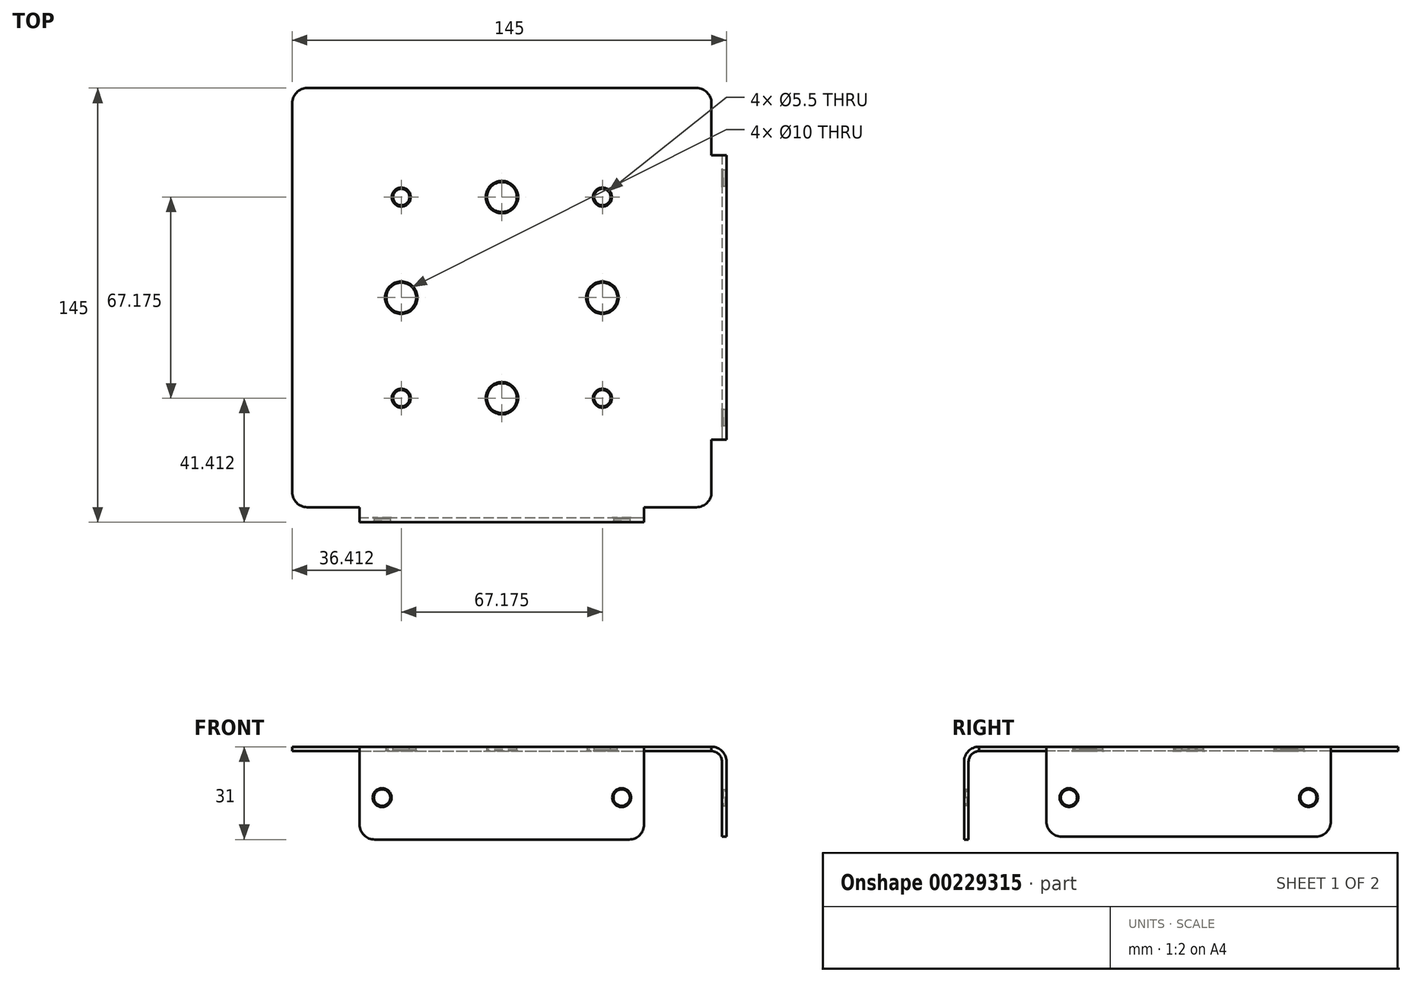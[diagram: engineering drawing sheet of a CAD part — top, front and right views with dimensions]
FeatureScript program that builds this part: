
annotation { "Feature Type Name" : "Feature", "Feature Type Description" : "" }
export const myFeature = defineFeature(function(context is Context, id is Id, definition is map)
    precondition{}
    {
        {
            var Q0;
            Q0=qCreatedBy(makeId("Top.planeOp"),FACE);
            var sketch = newSketch(context, id + "F0", { "sketchPlane" : qUnion([Q0])});
            skLineSegment(sketch, "E0.bottom", {"start": v(-70, 70) * mm, "end": v(70, 70) * mm});
            skLineSegment(sketch, "E0.top", {"start": v(-70, -70) * mm, "end": v(70, -70) * mm});
            skLineSegment(sketch, "E0.left", {"start": v(-70, 70) * mm, "end": v(-70, -70) * mm});
            skLineSegment(sketch, "E0.right", {"start": v(70, 70) * mm, "end": v(70, -70) * mm});
            skPoint(sketch, "E0.middle", {"position": v(0, 0) * mm});
            skLineSegment(sketch, "E1.bottom", {"start": v(-47.5, -70) * mm, "end": v(47.5, -70) * mm});
            skLineSegment(sketch, "E1.top", {"start": v(-47.5, -75) * mm, "end": v(47.5, -75) * mm});
            skLineSegment(sketch, "E1.left", {"start": v(-47.5, -70) * mm, "end": v(-47.5, -75) * mm});
            skLineSegment(sketch, "E1.right", {"start": v(47.5, -70) * mm, "end": v(47.5, -75) * mm});
            skLineSegment(sketch, "E2", {"start": v(70, -70) * mm, "end": v(0, 0) * mm, "construction": true});
            skLineSegment(sketch, "E3.MirrorCS", {"start": v(70, -47.5) * mm, "end": v(75, -47.5) * mm});
            skLineSegment(sketch, "E4.MirrorCS", {"start": v(70, 47.5) * mm, "end": v(70, -47.5) * mm});
            skLineSegment(sketch, "E5.MirrorCS", {"start": v(75, 47.5) * mm, "end": v(75, -47.5) * mm});
            skLineSegment(sketch, "E6.MirrorCS", {"start": v(70, 47.5) * mm, "end": v(75, 47.5) * mm});
            skSolve(sketch);
        }
        {
            var Q0;
            Q0=qSketchRegion(id+"F0",true);
            extrude(context, id + "F1", {"entities" : qUnion([Q0]), "depth" : 1.5 * mm});
        }
        {
            var Q0;
            Q0=makeQuery(id+"F1.opExtrude","CAP_FACE",FACE,{"disambiguationData":[OSD([sQuery(id+"F0.wireOp",EDGE,"E0.bottom"),sQuery(id+"F0.wireOp",EDGE,"E0.top"),sQuery(id+"F0.wireOp",EDGE,"E0.left"),sQuery(id+"F0.wireOp",EDGE,"E0.right")])],"isStart":false});
            var sketch = newSketch(context, id + "F2", { "sketchPlane" : qUnion([Q0])});
            skCircle(sketch, "E7", {"center": v(0, 0) * mm, "radius": 47.5 * mm, "construction": true});
            skCircle(sketch, "E8", {"center": v(-33.59, -33.59) * mm, "radius": 2.75 * mm});
            skLineSegment(sketch, "E9", {"start": v(0, 0) * mm, "end": v(-33.59, -33.59) * mm, "construction": true});
            skCircle(sketch, "E10.MirrorC", {"center": v(33.59, -33.59) * mm, "radius": 2.75 * mm});
            skCircle(sketch, "E11.MirrorC", {"center": v(-33.59, 33.59) * mm, "radius": 2.75 * mm});
            skCircle(sketch, "E12.MirrorC", {"center": v(33.59, 33.59) * mm, "radius": 2.75 * mm});
            skLineSegment(sketch, "E13", {"start": v(-33.59, -33.59) * mm, "end": v(33.59, -33.59) * mm, "construction": true});
            skLineSegment(sketch, "E14", {"start": v(33.59, 33.59) * mm, "end": v(33.59, -33.59) * mm, "construction": true});
            skCircle(sketch, "E15", {"center": v(0, -33.59) * mm, "radius": 5 * mm});
            skCircle(sketch, "E16", {"center": v(33.59, 0) * mm, "radius": 5 * mm});
            skCircle(sketch, "E17.MirrorC", {"center": v(-33.59, 0) * mm, "radius": 5 * mm});
            skCircle(sketch, "E18.MirrorC", {"center": v(0, 33.59) * mm, "radius": 5 * mm});
            skSolve(sketch);
        }
        {
            var Q0;
            Q0=qSketchRegion(id+"F2",true);
            extrude(context, id + "F3", {"entities" : qUnion([Q0]), "operationType" : NewBodyOperationType.REMOVE, "endBound" : BoundingType.THROUGH_ALL, "oppositeDirection" : true, "depth" : 25 * mm});
        }
        {
            var Q0;
            Q0=makeQuery(id+"F1.opExtrude","SWEPT_EDGE",EDGE,{"disambiguationData":[OSD([sQuery(id+"F0.wireOp",EDGE,"E0.top"),sQuery(id+"F0.wireOp",EDGE,"E0.right")])]});
            var Q1;
            Q1=makeQuery(id+"F1.opExtrude","SWEPT_EDGE",EDGE,{"disambiguationData":[OSD([sQuery(id+"F0.wireOp",EDGE,"E0.top"),sQuery(id+"F0.wireOp",EDGE,"E0.left")])]});
            var Q2;
            Q2=makeQuery(id+"F1.opExtrude","SWEPT_EDGE",EDGE,{"disambiguationData":[OSD([sQuery(id+"F0.wireOp",EDGE,"E0.bottom"),sQuery(id+"F0.wireOp",EDGE,"E0.right")])]});
            var Q3;
            Q3=makeQuery(id+"F1.opExtrude","SWEPT_EDGE",EDGE,{"disambiguationData":[OSD([sQuery(id+"F0.wireOp",EDGE,"E0.bottom"),sQuery(id+"F0.wireOp",EDGE,"E0.left")])]});
            fillet(context, id + "F4", {"entities" : qUnion([Q0, Q1, Q2, Q3]), "radius" : 5 * mm, "tangentPropagation" : true, "allowEdgeOverflow" : false});
        }
        {
            var Q0;
            Q0=makeQuery(id+"F1.opExtrude","CAP_VERTEX",VERTEX,{"disambiguationData":[OSD([sQuery(id+"F0.wireOp",EDGE,"E1.top"),sQuery(id+"F0.wireOp",EDGE,"E1.left")])],"isStart":false});
            var Q1;
            Q1=makeQuery(id+"F1.opExtrude","CAP_VERTEX",VERTEX,{"disambiguationData":[OSD([sQuery(id+"F0.wireOp",EDGE,"E1.top"),sQuery(id+"F0.wireOp",EDGE,"E1.right")])],"isStart":true});
            var Q2;
            Q2=makeQuery(id+"F1.opExtrude","CAP_VERTEX",VERTEX,{"disambiguationData":[OSD([sQuery(id+"F0.wireOp",EDGE,"E1.top"),sQuery(id+"F0.wireOp",EDGE,"E1.left")])],"isStart":true});
            cPlane(context, id + "F5", {"entities" : qUnion([Q0, Q1, Q2]), "cplaneType" : CPlaneType.THREE_POINT, "offset" : 25 * mm, "width" : 150 * mm, "height" : 150 * mm});
        }
        {
            var Q0;
            Q0=qCreatedBy(id+"F5.planeOp",FACE);
            var sketch = newSketch(context, id + "F6", { "sketchPlane" : qUnion([Q0])});
            skLineSegment(sketch, "E19.top", {"start": v(-47.5, -29.5) * mm, "end": v(47.5, -29.5) * mm});
            skLineSegment(sketch, "E19.left", {"start": v(-47.5, 1.5) * mm, "end": v(-47.5, -29.5) * mm});
            skLineSegment(sketch, "E19.right", {"start": v(47.5, 1.5) * mm, "end": v(47.5, -29.5) * mm});
            skCircle(sketch, "E20", {"center": v(-40, -15.5) * mm, "radius": 2.75 * mm});
            skCircle(sketch, "E21", {"center": v(40, -15.5) * mm, "radius": 2.75 * mm});
            skLineSegment(sketch, "E22", {"start": v(-47.5, 1.5) * mm, "end": v(47.5, 1.5) * mm});
            skSolve(sketch);
        }
        {
            var Q0;
            Q0=makeQuery(id+"F6.imprint","IMPRINT",FACE,{"disambiguationData":[TD([[makeQuery(id+"F6.imprint","IMPRINT",EDGE,{"derivedFrom":sQuery(id+"F6.wireOp",EDGE,"E19.top")}),1.0]])]});
            extrude(context, id + "F7", {"entities" : qUnion([Q0]), "operationType" : NewBodyOperationType.ADD, "oppositeDirection" : true, "depth" : 1.5 * mm});
        }
        {
            var Q0;
            Q0=makeQuery(id+"F1.opExtrude","CAP_VERTEX",VERTEX,{"disambiguationData":[OSD([sQuery(id+"F0.wireOp",EDGE,"E3.MirrorCS"),sQuery(id+"F0.wireOp",EDGE,"E5.MirrorCS")])],"isStart":false});
            var Q1;
            Q1=makeQuery(id+"F1.opExtrude","CAP_VERTEX",VERTEX,{"disambiguationData":[OSD([sQuery(id+"F0.wireOp",EDGE,"E3.MirrorCS"),sQuery(id+"F0.wireOp",EDGE,"E5.MirrorCS")])],"isStart":true});
            var Q2;
            Q2=makeQuery(id+"F1.opExtrude","CAP_VERTEX",VERTEX,{"disambiguationData":[OSD([sQuery(id+"F0.wireOp",EDGE,"E5.MirrorCS"),sQuery(id+"F0.wireOp",EDGE,"E6.MirrorCS")])],"isStart":false});
            cPlane(context, id + "F8", {"entities" : qUnion([Q0, Q1, Q2]), "cplaneType" : CPlaneType.THREE_POINT, "offset" : 25 * mm, "width" : 150 * mm, "height" : 150 * mm});
        }
        {
            var Q0;
            Q0=qCreatedBy(id+"F8.planeOp",FACE);
            var sketch = newSketch(context, id + "F9", { "sketchPlane" : qUnion([Q0])});
            skLineSegment(sketch, "E23.top", {"start": v(-47.5, -28.5) * mm, "end": v(47.5, -28.5) * mm});
            skLineSegment(sketch, "E23.left", {"start": v(-47.5, 1.5) * mm, "end": v(-47.5, -28.5) * mm});
            skLineSegment(sketch, "E23.right", {"start": v(47.5, 1.5) * mm, "end": v(47.5, -28.5) * mm});
            skCircle(sketch, "E24", {"center": v(-40, -15.5) * mm, "radius": 2.7 * mm});
            skCircle(sketch, "E25", {"center": v(40, -15.5) * mm, "radius": 2.7 * mm});
            skLineSegment(sketch, "E26", {"start": v(-47.5, 1.5) * mm, "end": v(47.5, 1.5) * mm});
            skSolve(sketch);
        }
        {
            var Q0;
            Q0=makeQuery(id+"F9.imprint","IMPRINT",FACE,{"disambiguationData":[TD([[makeQuery(id+"F9.imprint","IMPRINT",EDGE,{"derivedFrom":sQuery(id+"F9.wireOp",EDGE,"E23.top")}),1.0]])]});
            extrude(context, id + "F10", {"entities" : qUnion([Q0]), "operationType" : NewBodyOperationType.ADD, "depth" : 1.5 * mm});
        }
        {
            var Q0;
            Q0=makeQuery(id+"F1.opExtrude","CAP_EDGE",EDGE,{"disambiguationData":[OSD([sQuery(id+"F0.wireOp",EDGE,"E5.MirrorCS")])],"isStart":false});
            var Q1;
            Q1=makeQuery(id+"F1.opExtrude","CAP_EDGE",EDGE,{"disambiguationData":[OSD([sQuery(id+"F0.wireOp",EDGE,"E1.top")])],"isStart":false});
            fillet(context, id + "F11", {"entities" : qUnion([Q0, Q1]), "radius" : 5 * mm, "tangentPropagation" : true, "allowEdgeOverflow" : false});
        }
        {
            var Q0;
            Q0=makeQuery(id+"F10.boolean.opBoolean","INTERSECT",EDGE,{"derivedFrom":[makeQuery(id+"F1.opExtrude","CAP_FACE",FACE,{"disambiguationData":[OSD([sQuery(id+"F0.wireOp",EDGE,"E0.bottom"),sQuery(id+"F0.wireOp",EDGE,"E0.top"),sQuery(id+"F0.wireOp",EDGE,"E0.left"),sQuery(id+"F0.wireOp",EDGE,"E0.right"),sQuery(id+"F0.wireOp",EDGE,"E1.top"),sQuery(id+"F0.wireOp",EDGE,"E1.left"),sQuery(id+"F0.wireOp",EDGE,"E1.right"),sQuery(id+"F0.wireOp",EDGE,"E3.MirrorCS"),sQuery(id+"F0.wireOp",EDGE,"E5.MirrorCS"),sQuery(id+"F0.wireOp",EDGE,"E6.MirrorCS")])],"isStart":true}),makeQuery(id+"F10.opExtrude","CAP_FACE",FACE,{"disambiguationData":[OSD([sQuery(id+"F9.wireOp",EDGE,"E23.top"),sQuery(id+"F9.wireOp",EDGE,"E23.left"),sQuery(id+"F9.wireOp",EDGE,"E23.right"),sQuery(id+"F9.wireOp",EDGE,"E24"),sQuery(id+"F9.wireOp",EDGE,"E25"),sQuery(id+"F9.wireOp",EDGE,"E26")])],"isStart":false})]});
            var Q1;
            Q1=makeQuery(id+"F7.boolean.opBoolean","INTERSECT",EDGE,{"derivedFrom":[makeQuery(id+"F1.opExtrude","CAP_FACE",FACE,{"disambiguationData":[OSD([sQuery(id+"F0.wireOp",EDGE,"E0.bottom"),sQuery(id+"F0.wireOp",EDGE,"E0.top"),sQuery(id+"F0.wireOp",EDGE,"E0.left"),sQuery(id+"F0.wireOp",EDGE,"E0.right"),sQuery(id+"F0.wireOp",EDGE,"E1.top"),sQuery(id+"F0.wireOp",EDGE,"E1.left"),sQuery(id+"F0.wireOp",EDGE,"E1.right"),sQuery(id+"F0.wireOp",EDGE,"E3.MirrorCS"),sQuery(id+"F0.wireOp",EDGE,"E5.MirrorCS"),sQuery(id+"F0.wireOp",EDGE,"E6.MirrorCS")])],"isStart":true}),makeQuery(id+"F7.opExtrude","CAP_FACE",FACE,{"disambiguationData":[OSD([sQuery(id+"F6.wireOp",EDGE,"E19.top"),sQuery(id+"F6.wireOp",EDGE,"E19.left"),sQuery(id+"F6.wireOp",EDGE,"E19.right"),sQuery(id+"F6.wireOp",EDGE,"E20"),sQuery(id+"F6.wireOp",EDGE,"E21"),sQuery(id+"F6.wireOp",EDGE,"E22")])],"isStart":false})]});
            fillet(context, id + "F12", {"entities" : qUnion([Q0, Q1]), "radius" : 3.5 * mm, "tangentPropagation" : true, "allowEdgeOverflow" : false});
        }
        {
            var Q0;
            Q0=makeQuery(id+"F10.opExtrude","SWEPT_EDGE",EDGE,{"disambiguationData":[OSD([sQuery(id+"F9.wireOp",EDGE,"E23.top"),sQuery(id+"F9.wireOp",EDGE,"E23.right")])]});
            var Q1;
            Q1=makeQuery(id+"F7.opExtrude","SWEPT_EDGE",EDGE,{"disambiguationData":[OSD([sQuery(id+"F6.wireOp",EDGE,"E19.top"),sQuery(id+"F6.wireOp",EDGE,"E19.right")])]});
            var Q2;
            Q2=makeQuery(id+"F10.opExtrude","SWEPT_EDGE",EDGE,{"disambiguationData":[OSD([sQuery(id+"F9.wireOp",EDGE,"E23.top"),sQuery(id+"F9.wireOp",EDGE,"E23.left")])]});
            var Q3;
            Q3=makeQuery(id+"F7.opExtrude","SWEPT_EDGE",EDGE,{"disambiguationData":[OSD([sQuery(id+"F6.wireOp",EDGE,"E19.top"),sQuery(id+"F6.wireOp",EDGE,"E19.left")])]});
            fillet(context, id + "F13", {"entities" : qUnion([Q0, Q1, Q2, Q3]), "radius" : 5 * mm, "tangentPropagation" : true, "allowEdgeOverflow" : false});
        }
        {
            var Q0;
            Q0=makeQuery(id+"F3.boolean.opBoolean","COPY",FACE,{"derivedFrom":makeQuery(id+"F3.opExtrude","SWEPT_FACE",FACE,{"disambiguationData":[OSD([sQuery(id+"F2.wireOp",EDGE,"E15")])]})});
            var Q1;
            Q1=makeQuery(id+"F3.boolean.opBoolean","COPY",FACE,{"derivedFrom":makeQuery(id+"F3.opExtrude","SWEPT_FACE",FACE,{"disambiguationData":[OSD([sQuery(id+"F2.wireOp",EDGE,"E17.MirrorC")])]})});
            var Q2;
            Q2=makeQuery(id+"F3.boolean.opBoolean","COPY",FACE,{"derivedFrom":makeQuery(id+"F3.opExtrude","SWEPT_FACE",FACE,{"disambiguationData":[OSD([sQuery(id+"F2.wireOp",EDGE,"E8")])]})});
            var Q3;
            Q3=makeQuery(id+"F3.boolean.opBoolean","COPY",FACE,{"derivedFrom":makeQuery(id+"F3.opExtrude","SWEPT_FACE",FACE,{"disambiguationData":[OSD([sQuery(id+"F2.wireOp",EDGE,"E10.MirrorC")])]})});
            var Q4;
            Q4=makeQuery(id+"F3.boolean.opBoolean","COPY",FACE,{"derivedFrom":makeQuery(id+"F3.opExtrude","SWEPT_FACE",FACE,{"disambiguationData":[OSD([sQuery(id+"F2.wireOp",EDGE,"E16")])]})});
            var Q5;
            Q5=makeQuery(id+"F3.boolean.opBoolean","COPY",FACE,{"derivedFrom":makeQuery(id+"F3.opExtrude","SWEPT_FACE",FACE,{"disambiguationData":[OSD([sQuery(id+"F2.wireOp",EDGE,"E18.MirrorC")])]})});
            var Q6;
            Q6=makeQuery(id+"F3.boolean.opBoolean","COPY",FACE,{"derivedFrom":makeQuery(id+"F3.opExtrude","SWEPT_FACE",FACE,{"disambiguationData":[OSD([sQuery(id+"F2.wireOp",EDGE,"E11.MirrorC")])]})});
            var Q7;
            Q7=makeQuery(id+"F3.boolean.opBoolean","COPY",FACE,{"derivedFrom":makeQuery(id+"F3.opExtrude","SWEPT_FACE",FACE,{"disambiguationData":[OSD([sQuery(id+"F2.wireOp",EDGE,"E12.MirrorC")])]})});
            chamfer(context, id + "F14", {"entities" : qUnion([Q0, Q1, Q2, Q3, Q4, Q5, Q6, Q7]), "width" : 0.4 * mm, "tangentPropagation" : true});
        }
        {
            var Q0;
            Q0=makeQuery(id+"F7.opExtrude","SWEPT_FACE",FACE,{"disambiguationData":[OSD([sQuery(id+"F6.wireOp",EDGE,"E21")])]});
            var Q1;
            Q1=makeQuery(id+"F7.opExtrude","SWEPT_FACE",FACE,{"disambiguationData":[OSD([sQuery(id+"F6.wireOp",EDGE,"E20")])]});
            var Q2;
            Q2=makeQuery(id+"F10.opExtrude","SWEPT_FACE",FACE,{"disambiguationData":[OSD([sQuery(id+"F9.wireOp",EDGE,"E25")])]});
            var Q3;
            Q3=makeQuery(id+"F10.opExtrude","SWEPT_FACE",FACE,{"disambiguationData":[OSD([sQuery(id+"F9.wireOp",EDGE,"E24")])]});
            chamfer(context, id + "F15", {"entities" : qUnion([Q0, Q1, Q2, Q3]), "width" : 0.4 * mm, "tangentPropagation" : true});
        }
    });
